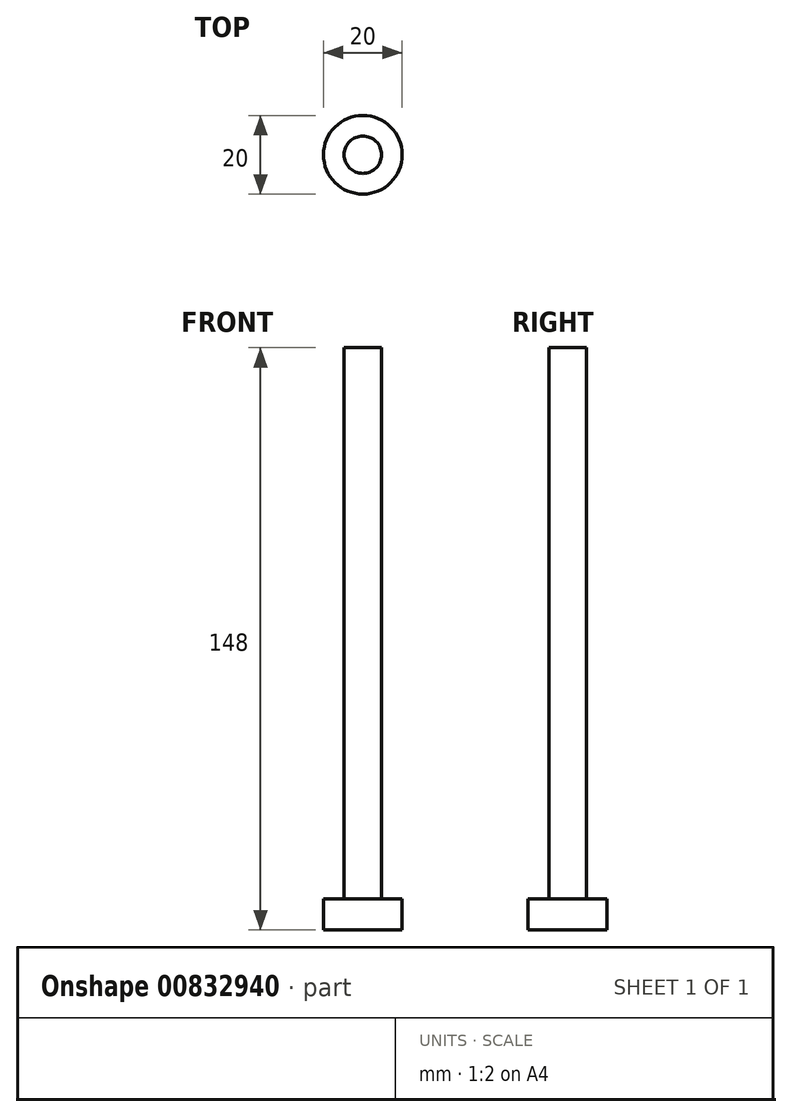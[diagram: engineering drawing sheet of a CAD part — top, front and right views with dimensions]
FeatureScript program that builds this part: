
annotation { "Feature Type Name" : "Feature", "Feature Type Description" : "" }
export const myFeature = defineFeature(function(context is Context, id is Id, definition is map)
    precondition{}
    {
        {
            var Q0;
            Q0=qCreatedBy(makeId("Top.planeOp"),FACE);
            var sketch = newSketch(context, id + "F0", { "sketchPlane" : qUnion([Q0])});
            skCircle(sketch, "E0", {"center": v(0, 0) * mm, "radius": 10 * mm});
            skSolve(sketch);
        }
        {
            var Q0;
            Q0 = qSketchRegion(id + "F0", true);
            extrude(context, id + "F1", {"entities" : qUnion([Q0]), "depth" : 8 * mm, "offsetDistance" : 25 * mm});
        }
        {
            var Q0;
            Q0=makeQuery(id+"F1.opExtrude","CAP_FACE",FACE,{"disambiguationData":[OSD([sQuery(id+"F0.wireOp",EDGE,"E0")])],"isStart":false});
            var sketch = newSketch(context, id + "F2", { "sketchPlane" : qUnion([Q0])});
            skSolve(sketch);
        }
        {
            var Q0;
            Q0=makeQuery(id+"F2.imprint","IMPRINT",FACE,{"disambiguationData":[TD([[makeQuery(id+"F2.imprint","IMPRINT",EDGE,{"derivedFrom":makeQuery(id+"F1.opExtrude","CAP_EDGE",EDGE,{"disambiguationData":[OSD([sQuery(id+"F0.wireOp",EDGE,"E0")])],"isStart":false})}),1.0]])]});
            var sketch = newSketch(context, id + "F3", { "sketchPlane" : qUnion([Q0])});
            skCircle(sketch, "E1", {"center": v(0, 0) * mm, "radius": 4.75 * mm});
            skSolve(sketch);
        }
        {
            var Q0;
            Q0 = qSketchRegion(id + "F3", true);
            extrude(context, id + "F4", {"entities" : qUnion([Q0]), "operationType" : NewBodyOperationType.ADD, "depth" : 140 * mm, "offsetDistance" : 25 * mm});
        }
    });
